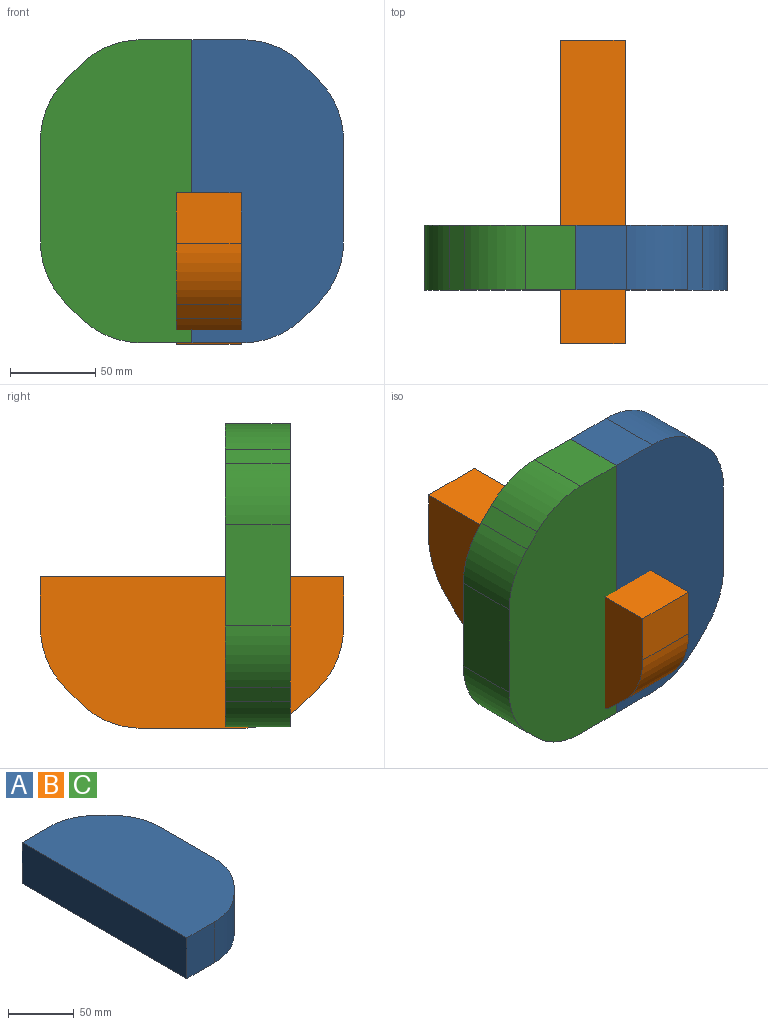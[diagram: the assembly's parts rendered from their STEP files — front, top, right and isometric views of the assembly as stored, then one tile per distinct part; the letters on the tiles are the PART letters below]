
ASSEMBLY  parts=3 mates=1
PART A: 12 faces, bbox 88.9x177.8x38.1 mm
  f0: plane 177.8x38.1mm, normal (-1,0,0), area 6774.2mm2, adj f1,f9,f10,f11
  f1: plane 38.1x29.76mm, normal (0,-1,0), area 1133.8mm2, adj f0,f2,f10,f11
  f2: cylinder r=50.8mm len=38.1mm, axis (0,0,-1), area 1520.1mm2, adj f1,f3,f10,f11
  f3: plane 38.1x8.34mm, normal (0.71,-0.71,0), area 449.5mm2, adj f2,f4,f10,f11
  f4: cylinder r=50.8mm len=38.1mm, axis (0,0,-1), area 1520.1mm2, adj f3,f5,f10,f11
  f5: plane 59.52x38.1mm, normal (1,0,0), area 2267.6mm2, adj f4,f6,f10,f11
  f6: cylinder r=50.8mm len=38.1mm, axis (0,0,-1), area 1520.1mm2, adj f5,f7,f10,f11
  f7: plane 38.1x8.34mm, normal (0.71,0.71,0), area 449.5mm2, adj f6,f8,f10,f11
  f8: cylinder r=50.8mm len=38.1mm, axis (0,0,-1), area 1520.1mm2, adj f7,f9,f10,f11
  f9: plane 38.1x29.76mm, normal (0,1,0), area 1133.8mm2, adj f0,f8,f10,f11
  f10: plane 177.8x88.9mm, normal (0,0,1), area 14132.7mm2, adj f0,f1,f2,f3,f4,f5,f6,f7
  f11: plane 177.8x88.9mm, normal (0,0,-1), area 14132.7mm2, adj f0,f1,f2,f3,f4,f5,f6,f7
PART B: same geometry as A
PART C: same geometry as A
PLACE A rot(axis=(-1,0,0),90deg) t=(290.5,-45,15.95)mm
PLACE B rot(axis=(0,1,0),90deg) t=(281.25,12.66,15.09)mm
PLACE C rot(axis=(0,0.71,-0.71),180deg) t=(290.5,-6.9,15.95)mm
MATE fastened A.f0 <-> C.f0  axis (-1,0,0) through (290.5,-25.95,15.95)mm
